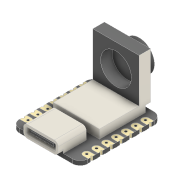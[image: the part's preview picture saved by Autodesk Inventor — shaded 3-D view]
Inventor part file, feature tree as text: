
AUTODESK INVENTOR PART (.ipt)
format: ipt  version: 2022 (Build 260153000, 153)  size: 304,128 bytes
history: native  units: mm
features: extrude x2, sketch x2, projected_geometry x2
ambient origin geometry x8: Origin, YZ Plane, XZ Plane, XY Plane, X Axis, Y Axis, Z Axis, Center Point
bodies: Volumenkörper1 (feature_tree), Body1 (feature_tree)
feature tree (6):
  extrude  "Extrusion1"  Depth=3.0mm TaperAngle=0.0deg
  extrude  "Extrusion2"  Depth=12.0mm
  sketch  "Skizze1"  dims[d0=8.0mm d1=3.0mm d2=0.0mm]
  projected_geometry  "Projizierte Kontur1"
  sketch  "Skizze2"  dims[d3=12.0mm d4=12.0mm d5=3.0mm d6=0.0mm]
  projected_geometry  "Projizierte Kontur2"
